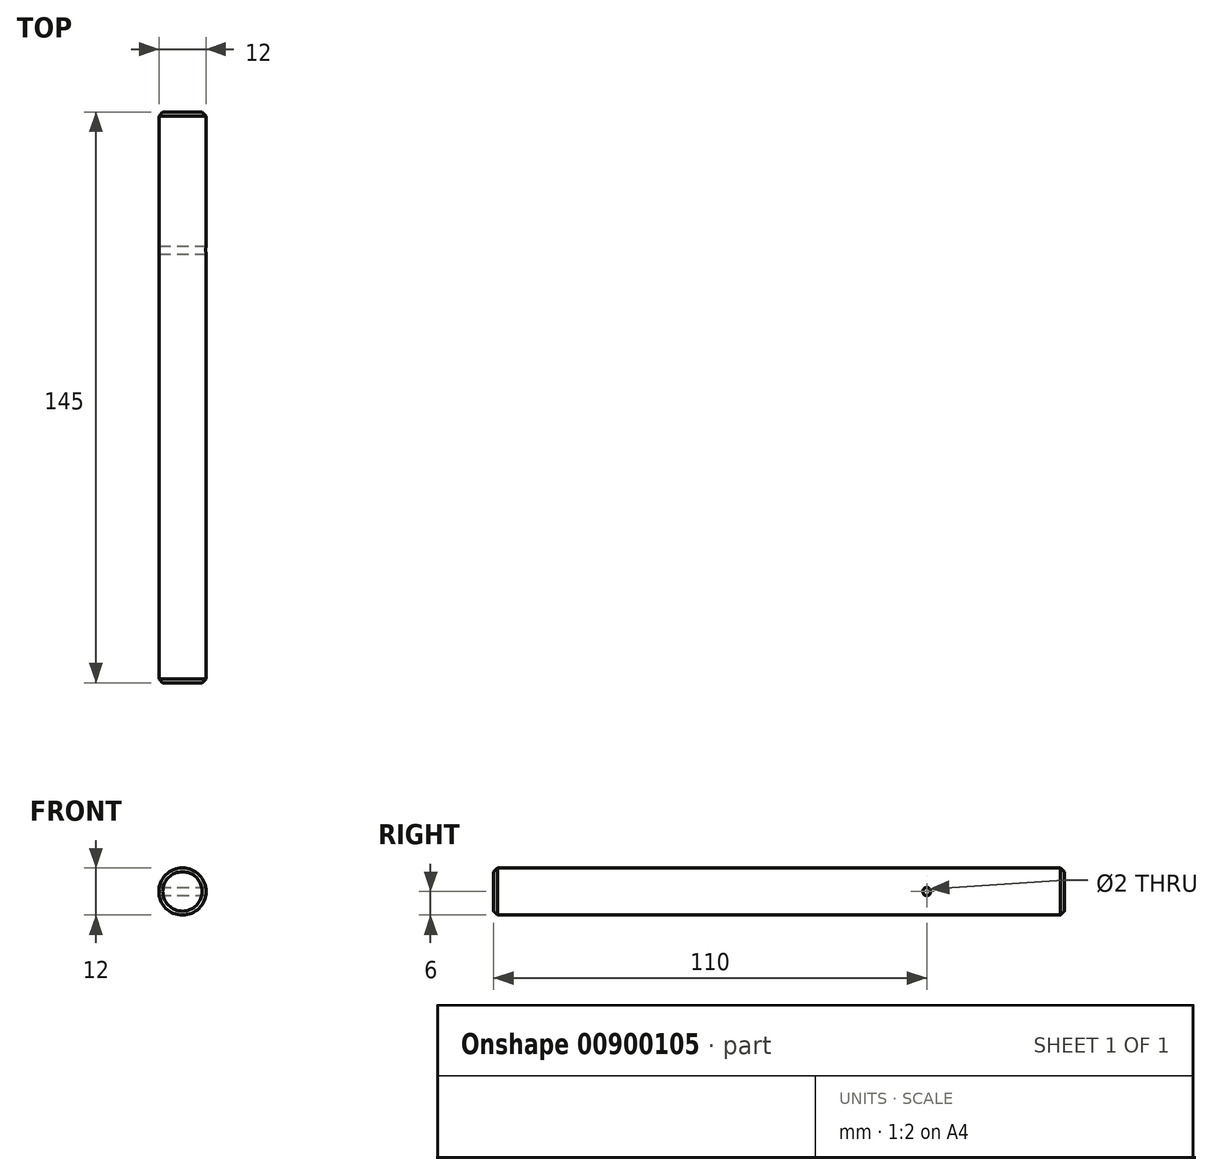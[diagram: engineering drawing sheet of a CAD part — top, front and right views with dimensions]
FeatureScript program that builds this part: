
annotation { "Feature Type Name" : "Feature", "Feature Type Description" : "" }
export const myFeature = defineFeature(function(context is Context, id is Id, definition is map)
    precondition{}
    {
        {
            var Q0;
            Q0=qCreatedBy(makeId("Front.planeOp"),FACE);
            var sketch = newSketch(context, id + "F0", { "sketchPlane" : qUnion([Q0])});
            skLineSegment(sketch, "E0", {"start": v(0, 0) * mm, "end": v(0, 6) * mm});
            skLineSegment(sketch, "E1", {"start": v(0, 0) * mm, "end": v(0, -6) * mm});
            skLineSegment(sketch, "E2", {"start": v(0, 0) * mm, "end": v(-6, 0) * mm});
            skArc(sketch, "E3", {"start": v(0, 6) * mm, "mid": v(-6, 0) * mm, "end": v(0, -6) * mm});
            skSolve(sketch);
        }
        {
            var Q0;
            Q0 = qSketchRegion(id + "F0", true);
            extrude(context, id + "F1", {"entities" : qUnion([Q0]), "oppositeDirection" : true, "depth" : 145 * mm, "offsetDistance" : 25 * mm});
        }
        {
            var Q0;
            Q0=makeQuery(id+"F1.opExtrude","SWEPT_FACE",FACE,{"disambiguationData":[OSD([sQuery(id+"F0.wireOp",EDGE,"E0"),sQuery(id+"F0.wireOp",EDGE,"E1")])]});
            var sketch = newSketch(context, id + "F2", { "sketchPlane" : qUnion([Q0])});
            skLineSegment(sketch, "E4", {"start": v(145, 9.21) * mm, "end": v(110, 9.21) * mm, "construction": true});
            skLineSegment(sketch, "E5", {"start": v(110, 6) * mm, "end": v(110, -6) * mm, "construction": true});
            skCircle(sketch, "E6", {"center": v(110, 0) * mm, "radius": 1 * mm});
            skSolve(sketch);
        }
        {
            var Q0;
            Q0 = qSketchRegion(id + "F2", true);
            extrude(context, id + "F3", {"entities" : qUnion([Q0]), "operationType" : NewBodyOperationType.REMOVE, "oppositeDirection" : true, "depth" : 25 * mm, "offsetDistance" : 25 * mm});
        }
        {
            var Q0;
            Q0=makeQuery(id+"F1.opExtrude","SWEPT_BODY",BODY,{"disambiguationData":[OSD([sQuery(id+"F0.wireOp",EDGE,"E0"),sQuery(id+"F0.wireOp",EDGE,"E1"),sQuery(id+"F0.wireOp",EDGE,"E3")])]});
            var Q1;
            Q1=makeQuery(id+"F1.opExtrude","SWEPT_FACE",FACE,{"disambiguationData":[OSD([sQuery(id+"F0.wireOp",EDGE,"E0"),sQuery(id+"F0.wireOp",EDGE,"E1")])]});
            mirror(context, id + "F4", {"operationType" : NewBodyOperationType.ADD, "entities" : qUnion([Q0]), "mirrorPlane" : qUnion([Q1])});
        }
        {
            var Q0;
            {var subQ0=makeQuery(id+"F1.opExtrude","CAP_EDGE",EDGE,{"disambiguationData":[OSD([sQuery(id+"F0.wireOp",EDGE,"E3")])],"isStart":false});Q0=makeQuery(id+"F4.boolean.opBoolean","MERGE",EDGE,{"derivedFrom":[subQ0,makeQuery(id+"F4.opPattern","COPY",EDGE,{"derivedFrom":subQ0,"instanceName":"1"})]});}
            var Q1;
            {var subQ0=makeQuery(id+"F1.opExtrude","CAP_EDGE",EDGE,{"disambiguationData":[OSD([sQuery(id+"F0.wireOp",EDGE,"E3")])],"isStart":true});Q1=makeQuery(id+"F4.boolean.opBoolean","MERGE",EDGE,{"derivedFrom":[subQ0,makeQuery(id+"F4.opPattern","COPY",EDGE,{"derivedFrom":subQ0,"instanceName":"1"})]});}
            chamfer(context, id + "F5", {"entities" : qUnion([Q0, Q1]), "chamferType" : ChamferType.OFFSET_ANGLE, "width" : 1 * mm, "oppositeDirection" : false, "angle" : 45 * degree, "tangentPropagation" : true});
        }
    });
